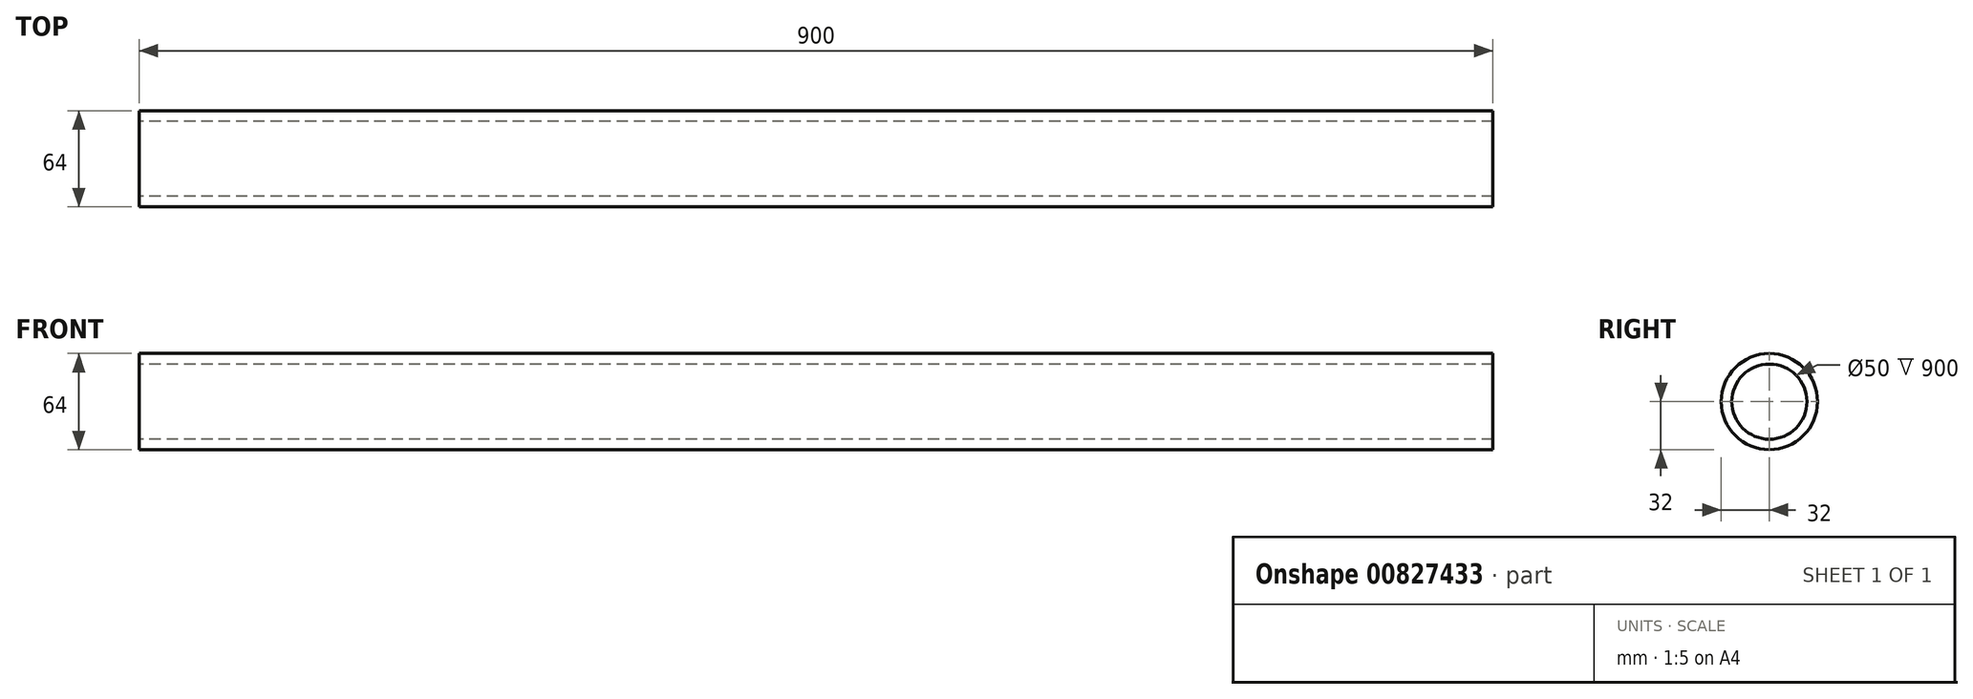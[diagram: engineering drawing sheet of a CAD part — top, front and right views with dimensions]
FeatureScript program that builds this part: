
annotation { "Feature Type Name" : "Feature", "Feature Type Description" : "" }
export const myFeature = defineFeature(function(context is Context, id is Id, definition is map)
    precondition{}
    {
        {
            var Q0;
            Q0=qCreatedBy(makeId("Right.planeOp"),FACE);
            var sketch = newSketch(context, id + "F0", { "sketchPlane" : qUnion([Q0])});
            skCircle(sketch, "E0", {"center": v(0, 0) * mm, "radius": 25 * mm});
            skCircle(sketch, "E1", {"center": v(0, 0) * mm, "radius": 32 * mm});
            skSolve(sketch);
        }
        {
            var Q0;
            Q0=makeQuery(id+"F0.imprint","IMPRINT",FACE,{"disambiguationData":[TD([[makeQuery(id+"F0.imprint","IMPRINT",EDGE,{"derivedFrom":sQuery(id+"F0.wireOp",EDGE,"E0")}),-1.0]])]});
            extrude(context, id + "F1", {"entities" : qUnion([Q0]), "depth" : 900 * mm, "offsetDistance" : 25 * mm});
        }
    });
